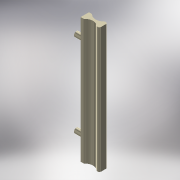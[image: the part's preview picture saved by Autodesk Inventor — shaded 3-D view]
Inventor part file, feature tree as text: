
AUTODESK INVENTOR PART (.ipt)
format: ipt  version: 2016 (Build 200138000, 138)  size: 164,352 bytes
history: native  units: mm
features: extrude x2, sketch x2, other x1, projected_geometry x1
ambient origin geometry x8: Origin, YZ Plane, XZ Plane, XY Plane, X Axis, Y Axis, Z Axis, Center Point
bodies: Body1 (feature_tree)
feature tree (6):
  other  "Sólido1"
  extrude  "Extrusión1"  Depth=150.0mm
  extrude  "Extrusion3"  TaperAngle=0.0deg  [1 undecoded]
  sketch  "Boceto1"  dims[d1=150.0mm d2=0.0mm d6=6.0mm]
  sketch  "Sketch3"  dims[d7=50.0mm d9=0.0mm]
  projected_geometry  "Projected Loop1"
note: 1 required parameter value undecoded (feature->parameter linkage not recoverable at this tier; creation-order binding heuristic only, values carry confidence <= 0.55)
